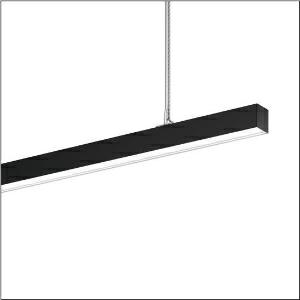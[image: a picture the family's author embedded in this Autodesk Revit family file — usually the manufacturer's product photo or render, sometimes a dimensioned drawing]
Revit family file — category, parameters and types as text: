
# Revit family: silica_21_51mx30da34bb
name_source: partatom
category: Lighting Fixtures
units: mm (PartAtom-declared; Revit-internal decimal feet)

## family parameters
Cut with Voids When Loaded = No
Host = Face
Light Source = No
Part Type = Normal
Room Calculation Point = No
Round Connector Dimension = Use Diameter
Shared = No

## types (1)
- --- (1 x LED, 4210 lm, 27.7 W, 3000K)
    Apparent Load = 28 VA
    CIE Flux Codes = 47 79 96 57 100
    Color Rendering = 80
    Color Temperature = 3000K
    Default Elevation = 1800 mm
    Description = Silica 21, office luminaire, primary optical cover: cover, of PMMA, opal, light emission: direct/indirect distribution, primary light characteristic: symmetric, installation type: suspended mounting, LED, rated luminous flux: 4.210lm, luminous efficacy: 152lm/W, light colour: 830, colour temperature: 3000K, control gear: DALI 2, with terminal, 3+2-pole, max. 2.5mm², mains connection: 220..240V, AC, 50/60Hz, rated input power: 27.7W, luminaire housing, of aluminium, matt jet black (RAL 9005), length: 1.204mm, width: 53mm, height: 53mm, protection rating (complete): IP20, insulation class (complete): insulation class I (protective earthing), certification: CE, permissible operating ambient temperature: 0..+35°C, standard: EN 50419, packaging unit: 1 piece
    Height = 53 mm
    Lamp = 1 x LED
    Lamp Light Flux = 4210 lm
    Lamp Power = 27.7 W
    Lamp count = 1
    Length = 1204 mm
    Luminous efficacy = 152 lm/W
    Manufacturer = Siteco
    ModVariant = No
    Model = 51MX30DA34BB
    Mounting Place = Ceiling
    Mounting Type = Pendant
    Number of Poles = 1
    OnlyDefault = Yes
    Power Factor = 1
    Product Name = Silica 21
    Product group = office luminaire | ceiling pendant
    ProductGroupID = 903
    Protection Class = Protection class I
    Protection Degree = IP 20
    RLX_Detail_Level = 1
    RLX_Emergency_Light_Flux = 0 lm
    RLX_Emergency_Type = 0
    RLX_Emergency_Type_DB = No
    RlxData = <blob elided: 26081 chars, md5=e31839f4>
    Socket = socket
    Standby Power = 0 W
    System Light Flux = 4210 lm
    System Power = 28 W
    Type Comments = factory setting: luminous flux: 100 % | dim-lin: 254 | 233 mA
    Type Image = l_1335856.jpg
    URL = http://relux.com
    VarID = @adj_119033
    Voltage = 0 V
    Weight = 0.00 kg
    Width = 53 mm

## geometry (parser evidence)
native form markers: Blend x4, Sweep x13
no freeform markers — native parametric forms only
